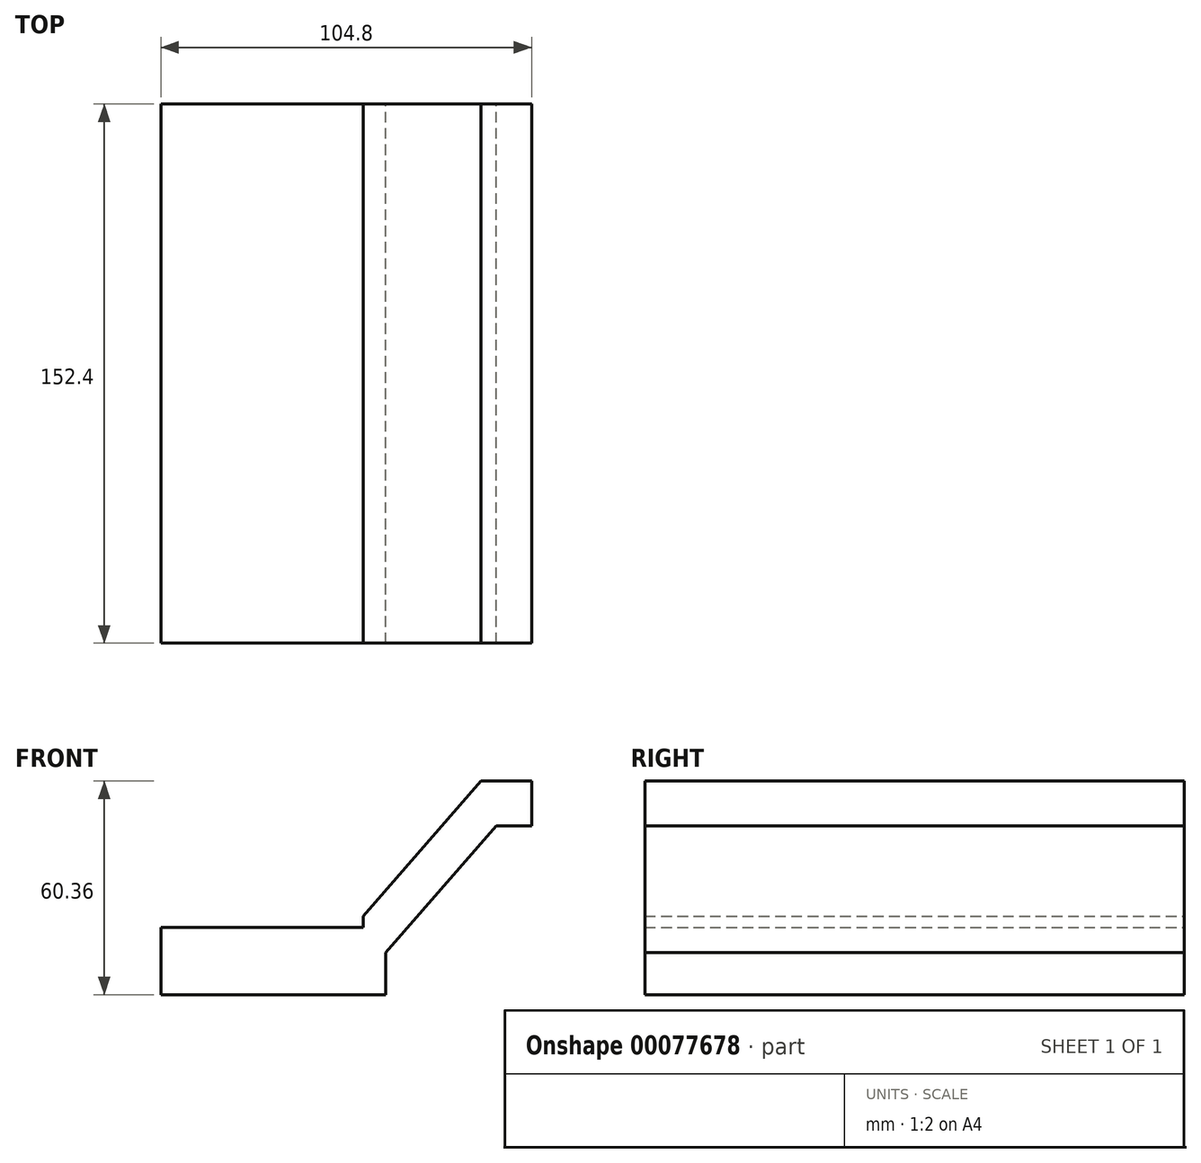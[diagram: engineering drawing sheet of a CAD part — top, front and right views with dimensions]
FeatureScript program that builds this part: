
annotation { "Feature Type Name" : "Feature", "Feature Type Description" : "" }
export const myFeature = defineFeature(function(context is Context, id is Id, definition is map)
    precondition{}
    {
        {
            var Q0;
            Q0=qCreatedBy(makeId("Front.planeOp"),FACE);
            var sketch = newSketch(context, id + "F0", { "sketchPlane" : qUnion([Q0])});
            skLineSegment(sketch, "E0", {"start": v(4.75, -30.18) * mm, "end": v(-52.4, -30.18) * mm});
            skLineSegment(sketch, "E1", {"start": v(-52.4, -30.18) * mm, "end": v(-52.4, -11.13) * mm});
            skLineSegment(sketch, "E2", {"start": v(-52.4, -11.13) * mm, "end": v(4.75, -11.13) * mm});
            skLineSegment(sketch, "E3", {"start": v(52.4, 30.18) * mm, "end": v(52.4, 17.47) * mm});
            skLineSegment(sketch, "E4", {"start": v(4.75, -30.18) * mm, "end": v(11.1, -30.18) * mm});
            skLineSegment(sketch, "E5", {"start": v(4.75, -30.18) * mm, "end": v(4.75, -7.94) * mm});
            skLineSegment(sketch, "E6", {"start": v(4.75, -7.94) * mm, "end": v(38.03, 30.18) * mm});
            skLineSegment(sketch, "E7", {"start": v(11.1, -18.32) * mm, "end": v(42.36, 17.47) * mm});
            skLineSegment(sketch, "E8", {"start": v(38.03, 30.18) * mm, "end": v(52.4, 30.18) * mm});
            skLineSegment(sketch, "E9", {"start": v(11.1, -30.18) * mm, "end": v(11.1, -18.32) * mm});
            skLineSegment(sketch, "E10", {"start": v(52.4, 17.47) * mm, "end": v(42.36, 17.47) * mm});
            skSolve(sketch);
        }
        {
            var Q0;
            Q0=makeQuery(id+"F0.imprint","IMPRINT",FACE,{"disambiguationData":[TD([[makeQuery(id+"F0.imprint","IMPRINT",EDGE,{"derivedFrom":sQuery(id+"F0.wireOp",EDGE,"E3")}),-1.0]])]});
            var Q1;
            {var subQ0=sQuery(id+"F0.wireOp",EDGE,"E0");Q1=makeQuery(id+"F0.imprint","IMPRINT",FACE,{"disambiguationData":[TD([[makeQuery(id+"F0.imprint","IMPRINT",EDGE,{"derivedFrom":subQ0}),-1.0]])]});}
            extrude(context, id + "F1", {"entities" : qUnion([Q0, Q1]), "depth" : 152.4 * mm});
        }
    });
